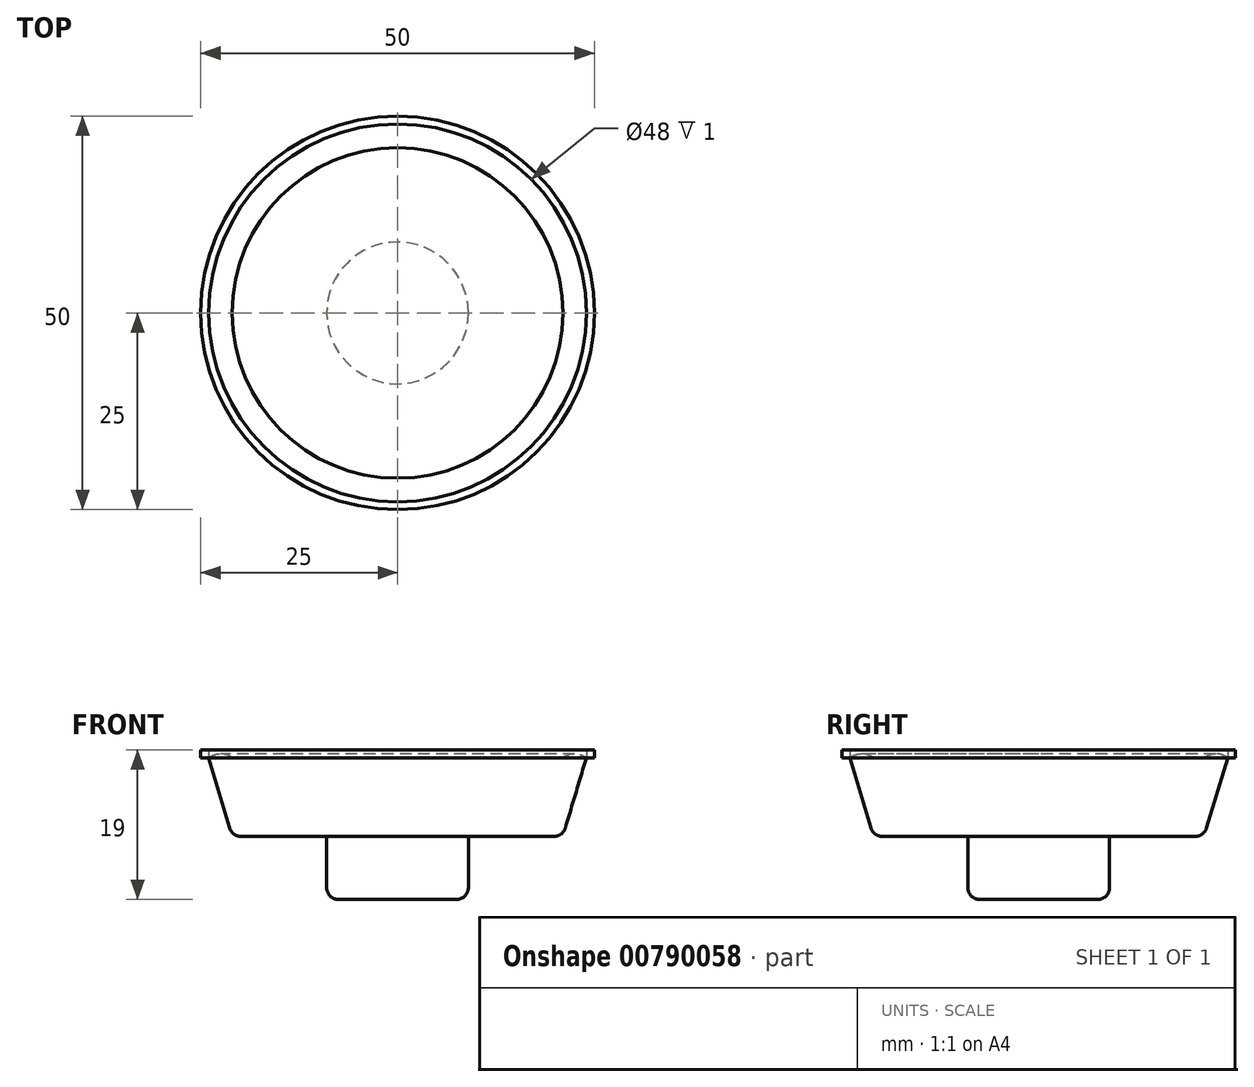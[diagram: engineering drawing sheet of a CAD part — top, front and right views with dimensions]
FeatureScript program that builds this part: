
annotation { "Feature Type Name" : "Feature", "Feature Type Description" : "" }
export const myFeature = defineFeature(function(context is Context, id is Id, definition is map)
    precondition{}
    {
        {
            var Q0;
            Q0=qCreatedBy(makeId("Top.planeOp"),FACE);
            var sketch = newSketch(context, id + "F0", { "sketchPlane" : qUnion([Q0])});
            skCircle(sketch, "E0", {"center": v(0, 0) * mm, "radius": 25 * mm});
            skCircle(sketch, "E1", {"center": v(0, 0) * mm, "radius": 9 * mm});
            skCircle(sketch, "E2.0", {"center": v(0, 0) * mm, "radius": 24 * mm});
            skCircle(sketch, "E3.0", {"center": v(0, 0) * mm, "radius": 21 * mm});
            skSolve(sketch);
        }
        {
            var Q0;
            Q0 = qSketchRegion(id + "F0", true);
            extrude(context, id + "F1", {"entities" : qUnion([Q0]), "depth" : 1 * mm, "offsetDistance" : 25 * mm});
        }
        {
            var Q0;
            Q0=makeQuery(id+"F0.imprint","IMPRINT",FACE,{"disambiguationData":[TD([[makeQuery(id+"F0.imprint","IMPRINT",EDGE,{"derivedFrom":sQuery(id+"F0.wireOp",EDGE,"E1")}),1.0]])]});
            extrude(context, id + "F2", {"entities" : qUnion([Q0]), "oppositeDirection" : true, "depth" : 18 * mm, "offsetDistance" : 25 * mm});
        }
        {
            var Q0;
            Q0=makeQuery(id+"F0.imprint","IMPRINT",FACE,{"disambiguationData":[TD([[makeQuery(id+"F0.imprint","IMPRINT",EDGE,{"derivedFrom":sQuery(id+"F0.wireOp",EDGE,"E2.0")}),1.0]])]});
            var Q1;
            Q1=makeQuery(id+"F0.imprint","IMPRINT",FACE,{"disambiguationData":[TD([[makeQuery(id+"F0.imprint","IMPRINT",EDGE,{"derivedFrom":sQuery(id+"F0.wireOp",EDGE,"E1")}),-1.0]])]});
            extrude(context, id + "F3", {"entities" : qUnion([Q0, Q1]), "operationType" : NewBodyOperationType.ADD, "oppositeDirection" : true, "depth" : 10 * mm, "offsetDistance" : 25 * mm});
        }
        {
            var Q0;
            Q0=makeQuery(id+"F0.imprint","IMPRINT",FACE,{"disambiguationData":[TD([[makeQuery(id+"F0.imprint","IMPRINT",EDGE,{"derivedFrom":sQuery(id+"F0.wireOp",EDGE,"E2.0")}),1.0]])]});
            extrude(context, id + "F4", {"entities" : qUnion([Q0]), "depth" : 0.5 * mm, "offsetDistance" : 25 * mm});
        }
        {
            var Q0;
            Q0=makeQuery(id+"F3.opExtrude","CAP_EDGE",EDGE,{"disambiguationData":[OSD([sQuery(id+"F0.wireOp",EDGE,"E2.0")])],"isStart":false});
            chamfer(context, id + "F5", {"entities" : qUnion([Q0]), "chamferType" : ChamferType.TWO_OFFSETS, "width1" : 10 * mm, "oppositeDirection" : false, "width2" : 3 * mm});
        }
        {
            var Q0;
            Q0=makeQuery(id+"F2.opExtrude","CAP_EDGE",EDGE,{"disambiguationData":[OSD([sQuery(id+"F0.wireOp",EDGE,"E1")])],"isStart":false});
            var Q1;
            {var subQ0=sQuery(id+"F0.wireOp",EDGE,"E2.0");Q1=makeQuery(id+"F5.opChamfer","BLEND_EDGE",EDGE,{"blendedFrom":[makeQuery(id+"F3.opExtrude","CAP_EDGE",EDGE,{"disambiguationData":[OSD([subQ0])],"isStart":false}),makeQuery(id+"F3.opExtrude","CAP_FACE",FACE,{"disambiguationData":[OSD([sQuery(id+"F0.wireOp",EDGE,"E1"),subQ0])],"isStart":false})],"blendedInto":[makeQuery(id+"F3.opExtrude","CAP_FACE",FACE,{"disambiguationData":[OSD([sQuery(id+"F0.wireOp",EDGE,"E1"),subQ0])],"isStart":false})]});}
            fillet(context, id + "F6", {"entities" : qUnion([Q0, Q1]), "radius" : 1.5 * mm, "tangentPropagation" : true, "allowEdgeOverflow" : false});
        }
        {
            var Q0;
            Q0=makeQuery(id+"F4.opExtrude","CAP_EDGE",EDGE,{"disambiguationData":[OSD([sQuery(id+"F0.wireOp",EDGE,"E2.0")])],"isStart":false});
            var Q1;
            Q1=makeQuery(id+"F4.opExtrude","CAP_EDGE",EDGE,{"disambiguationData":[OSD([sQuery(id+"F0.wireOp",EDGE,"E3.0")])],"isStart":false});
            fillet(context, id + "F7", {"entities" : qUnion([Q0, Q1]), "radius" : 2.5 * mm, "tangentPropagation" : true, "allowEdgeOverflow" : false});
        }
    });
